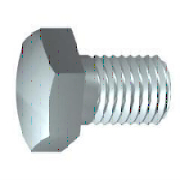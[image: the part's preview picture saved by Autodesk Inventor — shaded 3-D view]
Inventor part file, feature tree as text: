
AUTODESK INVENTOR PART (.ipt)
format: ipt  version: 2023 (Build 270158000, 158)  size: 216,064 bytes
history: native  units: mm
features: sketch x4, other x2, plane x1
ambient origin geometry x8: Origin, YZ Plane, XZ Plane, XY Plane, X Axis, Y Axis, Z Axis, Center Point
bodies: Solid1 (feature_tree)
feature tree (7):
  plane  "Work Plane1"
  sketch  "Sketch1"  dims[d6=0.6mm]
  sketch  "Sketch2"  dims[d7=11.63mm]
  sketch  "Sketch4"  dims[d9=135.0deg d10=8.0mm d11=35.0mm d13=90.0deg d14=22.0mm d15=0.0mm d16=0.6mm d17=2.0mm d18=45.0deg d19=13.0mm d20=15.011107mm d21=4.7mm d22=0.0mm d32=9.2mm d34=0.0mm d35=8.0mm d36=0.0mm d37=0.0mm d38=0.0mm d39=120.0deg d40=13.0mm d41=10.0mm d42=60.0deg d49=0.6mm]
  other  "Srf2"
  sketch  "Sketch3"  dims[d8=0.1mm]
  other  "Srf1"
